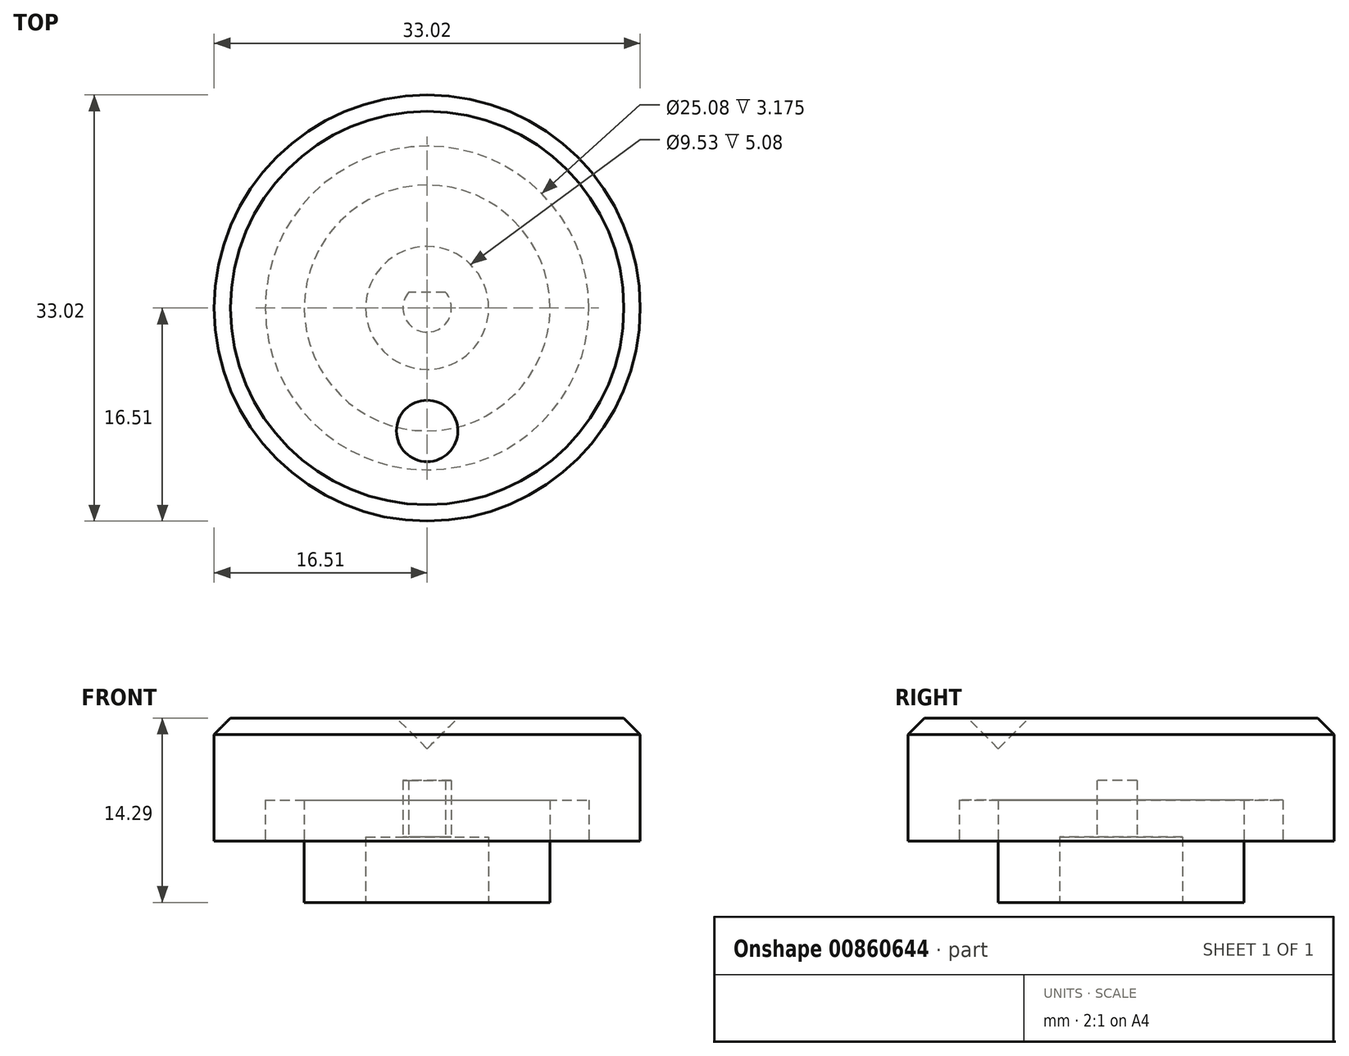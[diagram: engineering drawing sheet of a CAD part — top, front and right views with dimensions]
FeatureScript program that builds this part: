
annotation { "Feature Type Name" : "Feature", "Feature Type Description" : "" }
export const myFeature = defineFeature(function(context is Context, id is Id, definition is map)
    precondition{}
    {
        {
            var Q0;
            Q0=qCreatedBy(makeId("Right.planeOp"),FACE);
            var sketch = newSketch(context, id + "F0", { "sketchPlane" : qUnion([Q0])});
            skLineSegment(sketch, "E0", {"start": v(0, 0) * mm, "end": v(-16.51, 0) * mm});
            skLineSegment(sketch, "E1", {"start": v(-16.51, 0) * mm, "end": v(-16.51, -9.53) * mm});
            skLineSegment(sketch, "E2", {"start": v(-16.51, -9.53) * mm, "end": v(-12.54, -9.53) * mm});
            skLineSegment(sketch, "E3", {"start": v(-12.54, -9.53) * mm, "end": v(-12.54, -6.35) * mm});
            skLineSegment(sketch, "E4", {"start": v(-12.54, -6.35) * mm, "end": v(-9.53, -6.35) * mm});
            skLineSegment(sketch, "E5", {"start": v(-9.53, -6.35) * mm, "end": v(-9.53, -14.29) * mm});
            skLineSegment(sketch, "E6", {"start": v(-9.53, -14.29) * mm, "end": v(0, -14.29) * mm});
            skLineSegment(sketch, "E7", {"start": v(0, -14.29) * mm, "end": v(0, 0) * mm});
            skSolve(sketch);
        }
        {
            var Q0;
            Q0 = qSketchRegion(id + "F0", true);
            var Q1;
            Q1=sQuery(id+"F0.wireOp",EDGE,"E7");
            revolve(context, id + "F1", {"surfaceOperationType" : NewSurfaceOperationType.NEW, "entities" : qUnion([Q0]), "axis" : qUnion([Q1]), "revolveType" : RevolveType.FULL});
        }
        {
            var Q0;
            Q0=makeQuery(id+"F1.opRevolve","SWEPT_FACE",FACE,{"disambiguationData":[OSD([sQuery(id+"F0.wireOp",EDGE,"E6")])]});
            var sketch = newSketch(context, id + "F2", { "sketchPlane" : qUnion([Q0])});
            skArc(sketch, "E8", {"start": v(1.4, -1.14) * mm, "mid": v(0, 1.8) * mm, "end": v(-1.4, -1.14) * mm});
            skLineSegment(sketch, "E9", {"start": v(-1.4, -1.14) * mm, "end": v(1.4, -1.14) * mm});
            skLineSegment(sketch, "E10", {"start": v(0, -1.14) * mm, "end": v(0, 1.8) * mm, "construction": true});
            skSolve(sketch);
        }
        {
            var Q0;
            Q0 = qSketchRegion(id + "F2", true);
            extrude(context, id + "F3", {"entities" : qUnion([Q0]), "operationType" : NewBodyOperationType.REMOVE, "oppositeDirection" : true, "depth" : 9.46 * mm, "offsetDistance" : 25.4 * mm});
        }
        {
            var Q0;
            Q0=qCreatedBy(makeId("Right.planeOp"),FACE);
            var sketch = newSketch(context, id + "F4", { "sketchPlane" : qUnion([Q0])});
            skLineSegment(sketch, "E11", {"start": v(-11.9, 0) * mm, "end": v(-9.53, -2.38) * mm});
            skLineSegment(sketch, "E12", {"start": v(-9.53, -2.38) * mm, "end": v(-7.14, 0) * mm, "construction": true});
            skLineSegment(sketch, "E13", {"start": v(-7.14, 0) * mm, "end": v(-9.53, 0) * mm, "construction": true});
            skLineSegment(sketch, "E14", {"start": v(-9.53, 0) * mm, "end": v(-9.53, -2.38) * mm});
            skLineSegment(sketch, "E15", {"start": v(-9.53, 0) * mm, "end": v(-11.9, 0) * mm});
            skSolve(sketch);
        }
        {
            var Q0;
            Q0 = qSketchRegion(id + "F4", true);
            var Q1;
            Q1=sQuery(id+"F4.wireOp",EDGE,"E14");
            revolve(context, id + "F5", {"operationType" : NewBodyOperationType.REMOVE, "surfaceOperationType" : NewSurfaceOperationType.NEW, "entities" : qUnion([Q0]), "axis" : qUnion([Q1]), "revolveType" : RevolveType.FULL, "oppositeDirection" : true});
        }
        {
            var Q0;
            Q0=makeQuery(id+"F1.opRevolve","SWEPT_EDGE",EDGE,{"disambiguationData":[OSD([sQuery(id+"F0.wireOp",EDGE,"E0"),sQuery(id+"F0.wireOp",EDGE,"E1")])]});
            chamfer(context, id + "F6", {"entities" : qUnion([Q0]), "width" : 1.27 * mm, "tangentPropagation" : true});
        }
        {
            var Q0;
            Q0=makeQuery(id+"F1.opRevolve","SWEPT_FACE",FACE,{"disambiguationData":[OSD([sQuery(id+"F0.wireOp",EDGE,"E6")])]});
            var sketch = newSketch(context, id + "F7", { "sketchPlane" : qUnion([Q0])});
            skCircle(sketch, "E16", {"center": v(0, 0) * mm, "radius": 4.76 * mm});
            skSolve(sketch);
        }
        {
            var Q0;
            Q0 = qSketchRegion(id + "F7", true);
            extrude(context, id + "F8", {"entities" : qUnion([Q0]), "operationType" : NewBodyOperationType.REMOVE, "oppositeDirection" : true, "depth" : 5.08 * mm, "offsetDistance" : 25.4 * mm});
        }
        {
            var Q0;
            Q0=makeQuery(id+"F8.boolean.opBoolean","COPY",FACE,{"derivedFrom":makeQuery(id+"F8.opExtrude","CAP_FACE",FACE,{"disambiguationData":[OSD([sQuery(id+"F7.wireOp",EDGE,"E16")])],"isStart":false})});
            var sketch = newSketch(context, id + "F9", { "sketchPlane" : qUnion([Q0])});
            skLineSegment(sketch, "E17.0", {"start": v(1.43, -1.22) * mm, "end": v(-1.43, -1.22) * mm});
            skArc(sketch, "E17.1", {"start": v(-1.43, -1.22) * mm, "mid": v(0, 1.88) * mm, "end": v(1.43, -1.22) * mm});
            skSolve(sketch);
        }
        {
            var Q0;
            Q0 = qSketchRegion(id + "F9", true);
            var Q1;
            Q1=makeQuery(id+"F3.boolean.opBoolean","COPY",FACE,{"derivedFrom":makeQuery(id+"F3.opExtrude","CAP_FACE",FACE,{"disambiguationData":[OSD([sQuery(id+"F2.wireOp",EDGE,"E8"),sQuery(id+"F2.wireOp",EDGE,"E9")])],"isStart":false})});
            extrude(context, id + "F10", {"entities" : qUnion([Q0]), "operationType" : NewBodyOperationType.REMOVE, "endBound" : BoundingType.UP_TO_SURFACE, "oppositeDirection" : true, "depth" : 25.4 * mm, "endBoundEntityFace" : qUnion([Q1]), "offsetDistance" : 25.4 * mm});
        }
    });
